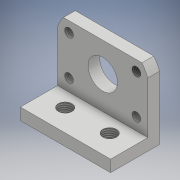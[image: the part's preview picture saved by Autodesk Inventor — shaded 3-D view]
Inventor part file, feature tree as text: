
AUTODESK INVENTOR PART (.ipt)
format: ipt  version: 2018 (Build 220112000, 112)  size: 165,888 bytes
history: native  units: mm
features: thread x7, sketch x6, extrude x3, hole x3
ambient origin geometry x8: Origin, YZ Plane, XZ Plane, XY Plane, X Axis, Y Axis, Z Axis, Center Point
bodies: Solid1 (feature_tree)
feature tree (19):
  extrude  "Extrusion1"  Depth=25.0mm
  hole  "Hole1"  [1 undecoded]
  extrude  "Extrusion2"  Depth=6.0mm
  hole  "Hole2"  [1 undecoded]
  hole  "Hole3"  [1 undecoded]
  extrude  "Extrusion3"  Depth=10.0mm
  thread  "Thread5"  [1 undecoded]
  thread  "Thread6"  [1 undecoded]
  thread  "Thread7"  [1 undecoded]
  thread  "Thread8"  [1 undecoded]
  thread  "Thread9"  [1 undecoded]
  thread  "Thread10"  [1 undecoded]
  thread  "Thread11"  [1 undecoded]
  sketch  "Sketch1"  dims[d0=46.0mm d1=25.0mm]
  sketch  "Sketch2"  dims[d2=6.0mm d3=0.0mm d5=13.8mm]
  sketch  "Sketch3"  dims[d6=7.0mm d7=6.0mm d8=4.0mm d9=2.0mm d10=90.0deg d11=8.0mm d12=20.594885mm d13=6.0mm]
  sketch  "Sketch4"  dims[d14=31.55mm d15=0.0mm d16=12.254mm]
  sketch  "Sketch5"  dims[d17=5.824mm d18=20.0mm]
  sketch  "Sketch6"  dims[d19=4.5mm d20=6.0mm d21=4.0mm d22=2.0mm d23=90.0deg d24=6.0mm d25=20.594885mm d26=15.0mm d27=15.0mm d28=6.0mm d29=4.0mm d30=2.0mm d31=90.0deg d32=6.0mm d33=20.594885mm d34=11.65mm d35=50.0mm d36=23.55mm d37=0.0mm d46=10.0mm d47=0.0mm d48=10.0mm d49=0.0mm d50=10.0mm d51=0.0mm d52=10.0mm d53=0.0mm d54=10.0mm d55=0.0mm d56=10.0mm d57=0.0mm d58=10.0mm d59=0.0mm]
note: 10 required parameter values undecoded (feature->parameter linkage not recoverable at this tier; creation-order binding heuristic only, values carry confidence <= 0.55)
